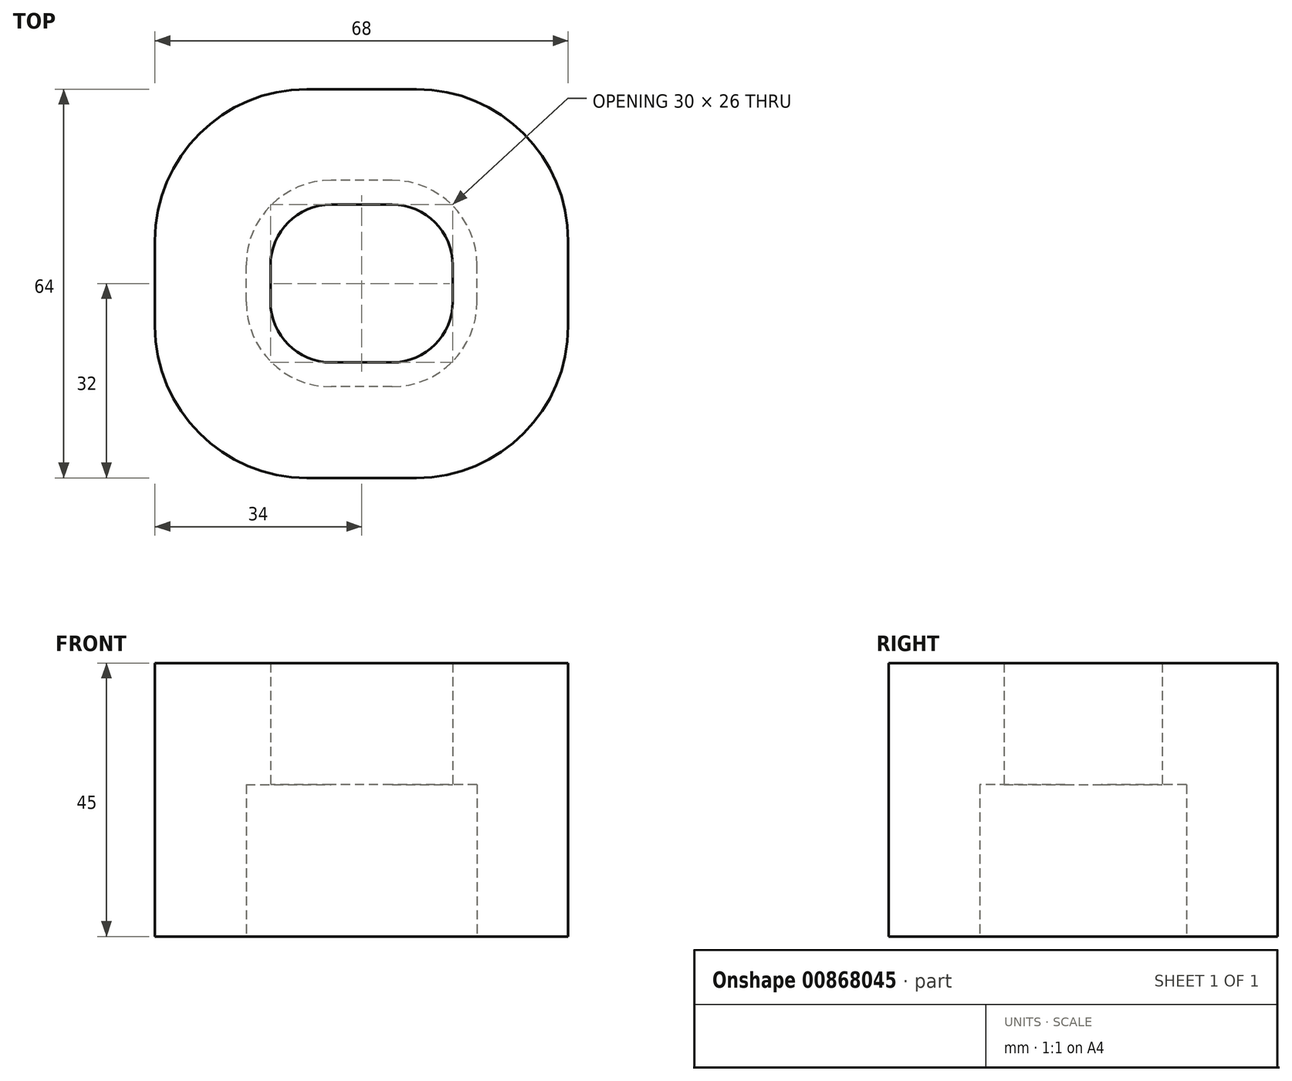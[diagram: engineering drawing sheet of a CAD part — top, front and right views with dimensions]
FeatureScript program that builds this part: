
annotation { "Feature Type Name" : "Feature", "Feature Type Description" : "" }
export const myFeature = defineFeature(function(context is Context, id is Id, definition is map)
    precondition{}
    {
        {
            var Q0;
            Q0=qCreatedBy(makeId("Top.planeOp"),FACE);
            var sketch = newSketch(context, id + "F0", { "sketchPlane" : qUnion([Q0])});
            skLineSegment(sketch, "E0.bottom", {"start": v(34, -32) * mm, "end": v(-34, -32) * mm});
            skLineSegment(sketch, "E0.top", {"start": v(34, 32) * mm, "end": v(-34, 32) * mm});
            skLineSegment(sketch, "E0.left", {"start": v(34, -32) * mm, "end": v(34, 32) * mm});
            skLineSegment(sketch, "E0.right", {"start": v(-34, -32) * mm, "end": v(-34, 32) * mm});
            skPoint(sketch, "E0.middle", {"position": v(0, 0) * mm});
            skLineSegment(sketch, "E1.bottom", {"start": v(19, -17) * mm, "end": v(-19, -17) * mm});
            skLineSegment(sketch, "E1.top", {"start": v(19, 17) * mm, "end": v(-19, 17) * mm});
            skLineSegment(sketch, "E1.left", {"start": v(19, -17) * mm, "end": v(19, 17) * mm});
            skLineSegment(sketch, "E1.right", {"start": v(-19, -17) * mm, "end": v(-19, 17) * mm});
            skSolve(sketch);
        }
        {
            var Q0;
            Q0=makeQuery(id+"F0.imprint","IMPRINT",FACE,{"disambiguationData":[TD([[makeQuery(id+"F0.imprint","IMPRINT",EDGE,{"derivedFrom":sQuery(id+"F0.wireOp",EDGE,"E0.bottom")}),-1.0]])]});
            extrude(context, id + "F1", {"entities" : qUnion([Q0]), "depth" : 25 * mm, "offsetDistance" : 25 * mm});
        }
        {
            var Q0;
            Q0=makeQuery(id+"F1.opExtrude","CAP_FACE",FACE,{"disambiguationData":[OSD([sQuery(id+"F0.wireOp",EDGE,"E0.bottom"),sQuery(id+"F0.wireOp",EDGE,"E0.top"),sQuery(id+"F0.wireOp",EDGE,"E0.left"),sQuery(id+"F0.wireOp",EDGE,"E0.right"),sQuery(id+"F0.wireOp",EDGE,"E1.bottom"),sQuery(id+"F0.wireOp",EDGE,"E1.top"),sQuery(id+"F0.wireOp",EDGE,"E1.left"),sQuery(id+"F0.wireOp",EDGE,"E1.right")])],"isStart":false});
            var sketch = newSketch(context, id + "F2", { "sketchPlane" : qUnion([Q0])});
            skLineSegment(sketch, "E2.0", {"start": v(-15, -13) * mm, "end": v(-15, 13) * mm});
            skLineSegment(sketch, "E2.1", {"start": v(15, -13) * mm, "end": v(-15, -13) * mm});
            skLineSegment(sketch, "E2.2", {"start": v(15, -13) * mm, "end": v(15, 13) * mm});
            skLineSegment(sketch, "E2.3", {"start": v(15, 13) * mm, "end": v(-15, 13) * mm});
            skSolve(sketch);
        }
        {
            var Q0;
            Q0=makeQuery(id+"F2.imprint","IMPRINT",FACE,{"disambiguationData":[TD([[makeQuery(id+"F2.imprint","IMPRINT",EDGE,{"derivedFrom":sQuery(id+"F2.wireOp",EDGE,"E2.0")}),1.0]])]});
            var Q1;
            Q1=makeQuery(id+"F2.imprint","IMPRINT",FACE,{"disambiguationData":[TD([[makeQuery(id+"F2.imprint","IMPRINT",EDGE,{"derivedFrom":makeQuery(id+"F1.opExtrude","CAP_EDGE",EDGE,{"disambiguationData":[OSD([sQuery(id+"F0.wireOp",EDGE,"E0.bottom")])],"isStart":false})}),-1.0]])]});
            extrude(context, id + "F3", {"entities" : qUnion([Q0, Q1]), "operationType" : NewBodyOperationType.ADD, "depth" : 20 * mm, "offsetDistance" : 25 * mm});
        }
        {
            var Q0;
            Q0=makeQuery(id+"F3.opExtrude","SWEPT_EDGE",EDGE,{"disambiguationData":[OSD([sQuery(id+"F2.wireOp",EDGE,"E2.0"),sQuery(id+"F2.wireOp",EDGE,"E2.3")])]});
            var Q1;
            Q1=makeQuery(id+"F3.opExtrude","SWEPT_EDGE",EDGE,{"disambiguationData":[OSD([sQuery(id+"F2.wireOp",EDGE,"E2.0"),sQuery(id+"F2.wireOp",EDGE,"E2.1")])]});
            var Q2;
            Q2=makeQuery(id+"F3.opExtrude","SWEPT_EDGE",EDGE,{"disambiguationData":[OSD([sQuery(id+"F2.wireOp",EDGE,"E2.1"),sQuery(id+"F2.wireOp",EDGE,"E2.2")])]});
            var Q3;
            Q3=makeQuery(id+"F3.opExtrude","SWEPT_EDGE",EDGE,{"disambiguationData":[OSD([sQuery(id+"F2.wireOp",EDGE,"E2.2"),sQuery(id+"F2.wireOp",EDGE,"E2.3")])]});
            fillet(context, id + "F4", {"entities" : qUnion([Q0, Q1, Q2, Q3]), "radius" : 10 * mm, "tangentPropagation" : true, "allowEdgeOverflow" : false});
        }
        {
            var Q0;
            Q0=makeQuery(id+"F1.opExtrude","SWEPT_EDGE",EDGE,{"disambiguationData":[OSD([sQuery(id+"F0.wireOp",EDGE,"E1.bottom"),sQuery(id+"F0.wireOp",EDGE,"E1.left")])]});
            var Q1;
            Q1=makeQuery(id+"F1.opExtrude","SWEPT_EDGE",EDGE,{"disambiguationData":[OSD([sQuery(id+"F0.wireOp",EDGE,"E1.top"),sQuery(id+"F0.wireOp",EDGE,"E1.left")])]});
            var Q2;
            Q2=makeQuery(id+"F1.opExtrude","SWEPT_EDGE",EDGE,{"disambiguationData":[OSD([sQuery(id+"F0.wireOp",EDGE,"E1.top"),sQuery(id+"F0.wireOp",EDGE,"E1.right")])]});
            var Q3;
            Q3=makeQuery(id+"F1.opExtrude","SWEPT_EDGE",EDGE,{"disambiguationData":[OSD([sQuery(id+"F0.wireOp",EDGE,"E1.bottom"),sQuery(id+"F0.wireOp",EDGE,"E1.right")])]});
            fillet(context, id + "F5", {"entities" : qUnion([Q0, Q1, Q2, Q3]), "radius" : 14 * mm, "tangentPropagation" : true, "allowEdgeOverflow" : false});
        }
        {
            var Q0;
            {var subQ0=sQuery(id+"F0.wireOp",EDGE,"E0.left");var subQ1=sQuery(id+"F0.wireOp",EDGE,"E0.top");Q0=makeQuery(id+"F3.boolean.opBoolean","MERGE",EDGE,{"derivedFrom":[makeQuery(id+"F1.opExtrude","SWEPT_EDGE",EDGE,{"disambiguationData":[OSD([subQ1,subQ0])]}),makeQuery(id+"F3.opExtrude","SWEPT_EDGE",EDGE,{"disambiguationData":[OSD([subQ1,subQ0])]})]});}
            var Q1;
            {var subQ0=sQuery(id+"F0.wireOp",EDGE,"E0.right");var subQ1=sQuery(id+"F0.wireOp",EDGE,"E0.top");Q1=makeQuery(id+"F3.boolean.opBoolean","MERGE",EDGE,{"derivedFrom":[makeQuery(id+"F1.opExtrude","SWEPT_EDGE",EDGE,{"disambiguationData":[OSD([subQ1,subQ0])]}),makeQuery(id+"F3.opExtrude","SWEPT_EDGE",EDGE,{"disambiguationData":[OSD([subQ1,subQ0])]})]});}
            var Q2;
            {var subQ0=sQuery(id+"F0.wireOp",EDGE,"E0.left");var subQ1=sQuery(id+"F0.wireOp",EDGE,"E0.bottom");Q2=makeQuery(id+"F3.boolean.opBoolean","MERGE",EDGE,{"derivedFrom":[makeQuery(id+"F1.opExtrude","SWEPT_EDGE",EDGE,{"disambiguationData":[OSD([subQ1,subQ0])]}),makeQuery(id+"F3.opExtrude","SWEPT_EDGE",EDGE,{"disambiguationData":[OSD([subQ1,subQ0])]})]});}
            var Q3;
            {var subQ0=sQuery(id+"F0.wireOp",EDGE,"E0.right");var subQ1=sQuery(id+"F0.wireOp",EDGE,"E0.bottom");Q3=makeQuery(id+"F3.boolean.opBoolean","MERGE",EDGE,{"derivedFrom":[makeQuery(id+"F1.opExtrude","SWEPT_EDGE",EDGE,{"disambiguationData":[OSD([subQ1,subQ0])]}),makeQuery(id+"F3.opExtrude","SWEPT_EDGE",EDGE,{"disambiguationData":[OSD([subQ1,subQ0])]})]});}
            fillet(context, id + "F6", {"entities" : qUnion([Q0, Q1, Q2, Q3]), "radius" : 25 * mm, "tangentPropagation" : true, "allowEdgeOverflow" : false});
        }
    });
